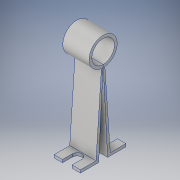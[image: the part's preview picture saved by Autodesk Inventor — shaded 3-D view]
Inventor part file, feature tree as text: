
AUTODESK INVENTOR PART (.ipt)
format: ipt  version: 2018 (Build 220112000, 112)  size: 146,432 bytes
history: native  units: in
note: dims shown in document units (in); Inventor stores cm internally (conversion verified against a paired STEP export)
features: extrude x2, sketch x2
ambient origin geometry x8: Origin, YZ Plane, XZ Plane, XY Plane, X Axis, Y Axis, Z Axis, Center Point
bodies: Solid1 (feature_tree)
feature tree (4):
  extrude  "Extrusion1"  Depth=0.31in
  extrude  "Extrusion2"  Depth=0.115in
  sketch  "Sketch2"  dims[d2=0.385in d3=0.31in]
  sketch  "Sketch3"  dims[d12=0.36in d13=0.0in d14=0.115in d15=0.115in d17=0.36in d18=0.0in]
